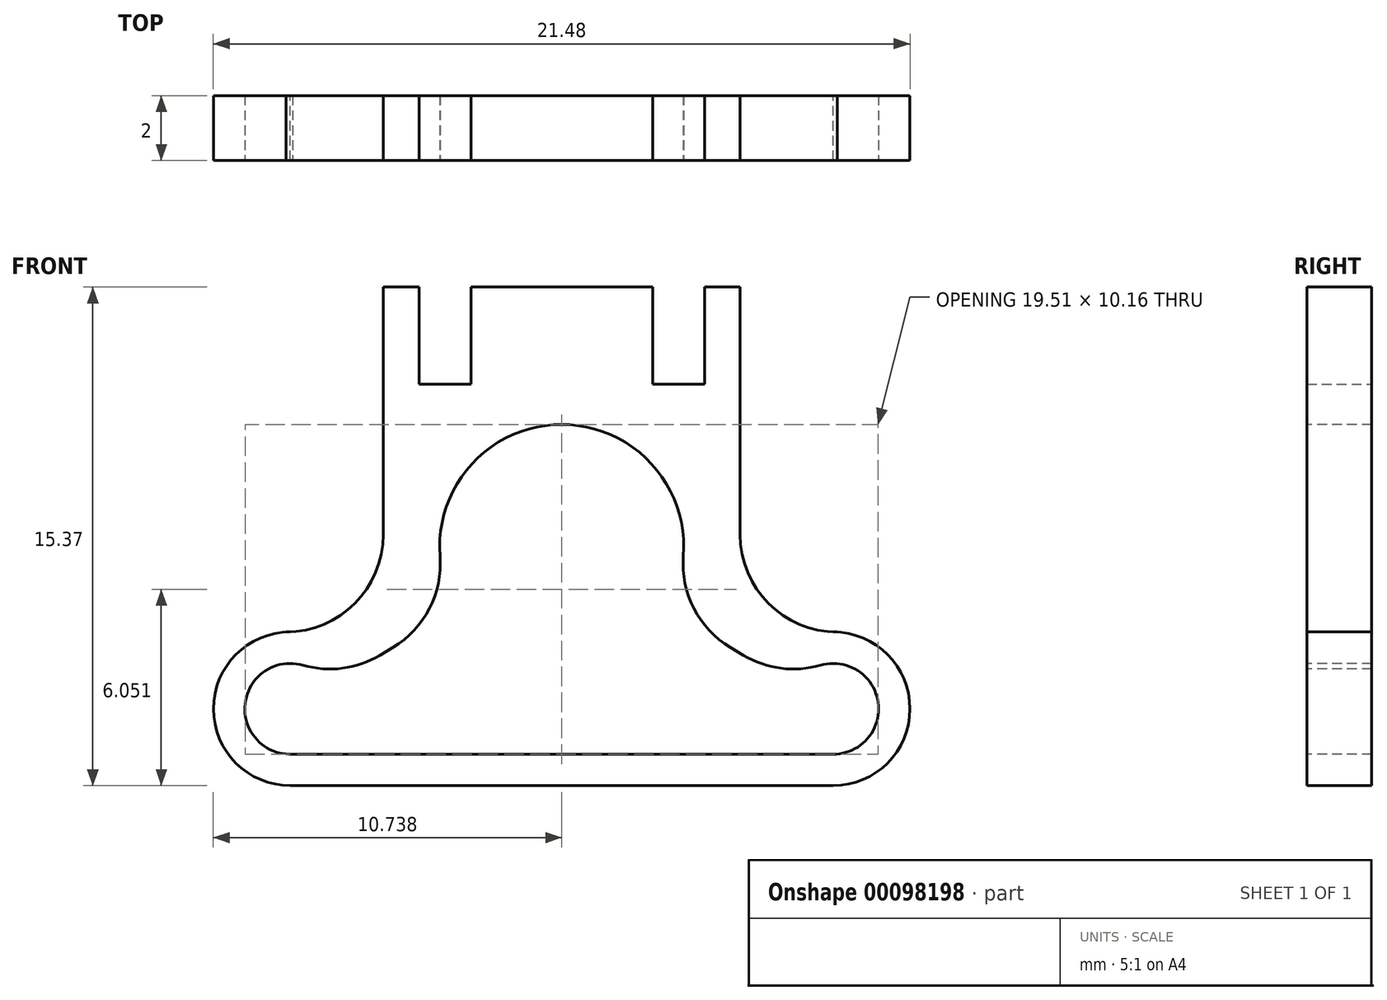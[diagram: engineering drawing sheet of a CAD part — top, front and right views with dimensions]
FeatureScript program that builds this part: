
annotation { "Feature Type Name" : "Feature", "Feature Type Description" : "" }
export const myFeature = defineFeature(function(context is Context, id is Id, definition is map)
    precondition{}
    {
        {
            var Q0;
            Q0=qCreatedBy(makeId("Front.planeOp"),FACE);
            var sketch = newSketch(context, id + "F0", { "sketchPlane" : qUnion([Q0])});
            skLineSegment(sketch, "E0.top", {"start": v(4.4, 5) * mm, "end": v(2.8, 5) * mm});
            skLineSegment(sketch, "E0.left", {"start": v(5.5, 0.37) * mm, "end": v(5.5, 5) * mm});
            skLineSegment(sketch, "E0.right", {"start": v(-5.5, 0.37) * mm, "end": v(-5.5, 5) * mm});
            skPoint(sketch, "E0.middle", {"position": v(0, 0) * mm});
            skLineSegment(sketch, "E1.bottom", {"start": v(8.37, -7.37) * mm, "end": v(-8.37, -7.37) * mm});
            skLineSegment(sketch, "E1.top", {"start": v(8.5, -2.63) * mm, "end": v(8.37, -2.63) * mm});
            skLineSegment(sketch, "E2.trimOffspring", {"start": v(-8.37, -2.63) * mm, "end": v(-8.5, -2.63) * mm});
            skArc(sketch, "E3.filletArc", {"start": v(-8.5, -2.63) * mm, "mid": v(-6.38, -1.75) * mm, "end": v(-5.5, 0.37) * mm});
            skArc(sketch, "E4.filletArc", {"start": v(5.5, 0.37) * mm, "mid": v(6.38, -1.75) * mm, "end": v(8.5, -2.63) * mm});
            skArc(sketch, "E5", {"start": v(-8.37, -2.63) * mm, "mid": v(-10.74, -5) * mm, "end": v(-8.37, -7.37) * mm});
            skArc(sketch, "E6", {"start": v(8.37, -7.37) * mm, "mid": v(10.74, -5) * mm, "end": v(8.37, -2.63) * mm});
            skLineSegment(sketch, "E7.bottom", {"start": v(2.8, 8) * mm, "end": v(-2.8, 8) * mm});
            skLineSegment(sketch, "E7.left", {"start": v(2.8, 8) * mm, "end": v(2.8, 5) * mm});
            skLineSegment(sketch, "E7.right", {"start": v(-2.8, 8) * mm, "end": v(-2.8, 5) * mm});
            skLineSegment(sketch, "E8", {"start": v(-5.5, 5) * mm, "end": v(-5.5, 8) * mm});
            skLineSegment(sketch, "E9", {"start": v(-5.5, 8) * mm, "end": v(-4.4, 8) * mm});
            skLineSegment(sketch, "E10", {"start": v(-4.4, 8) * mm, "end": v(-4.4, 5) * mm});
            skLineSegment(sketch, "E11.trimOffspring", {"start": v(-2.8, 5) * mm, "end": v(-4.4, 5) * mm});
            skLineSegment(sketch, "E12.MirrorCS", {"start": v(5.5, 8) * mm, "end": v(4.4, 8) * mm});
            skLineSegment(sketch, "E13.MirrorCS", {"start": v(4.4, 8) * mm, "end": v(4.4, 5) * mm});
            skLineSegment(sketch, "E14.MirrorCS", {"start": v(5.5, 5) * mm, "end": v(5.5, 8) * mm});
            skSolve(sketch);
        }
        {
            var Q0;
            Q0 = qSketchRegion(id + "F0", true);
            extrude(context, id + "F1", {"entities" : qUnion([Q0]), "depth" : 2 * mm});
        }
        {
            var Q0;
            Q0=makeQuery(id+"F1.opExtrude","CAP_FACE",FACE,{"disambiguationData":[OSD([sQuery(id+"F0.wireOp",EDGE,"E0.top"),sQuery(id+"F0.wireOp",EDGE,"E0.left"),sQuery(id+"F0.wireOp",EDGE,"E0.right"),sQuery(id+"F0.wireOp",EDGE,"E1.bottom"),sQuery(id+"F0.wireOp",EDGE,"E1.top"),sQuery(id+"F0.wireOp",EDGE,"E2.trimOffspring"),sQuery(id+"F0.wireOp",EDGE,"E3.filletArc"),sQuery(id+"F0.wireOp",EDGE,"E4.filletArc"),sQuery(id+"F0.wireOp",EDGE,"E5"),sQuery(id+"F0.wireOp",EDGE,"E6"),sQuery(id+"F0.wireOp",EDGE,"E7.bottom"),sQuery(id+"F0.wireOp",EDGE,"E7.left"),sQuery(id+"F0.wireOp",EDGE,"E7.right"),sQuery(id+"F0.wireOp",EDGE,"E8"),sQuery(id+"F0.wireOp",EDGE,"E9"),sQuery(id+"F0.wireOp",EDGE,"E10"),sQuery(id+"F0.wireOp",EDGE,"E11.trimOffspring"),sQuery(id+"F0.wireOp",EDGE,"E12.MirrorCS"),sQuery(id+"F0.wireOp",EDGE,"E13.MirrorCS"),sQuery(id+"F0.wireOp",EDGE,"E14.MirrorCS")])],"isStart":false});
            var sketch = newSketch(context, id + "F2", { "sketchPlane" : qUnion([Q0])});
            skArc(sketch, "E15", {"start": v(3.75, -0.3) * mm, "mid": v(0, 3.76) * mm, "end": v(-3.75, -0.3) * mm});
            skPoint(sketch, "E16.middle", {"position": v(0, -5.45) * mm});
            skArc(sketch, "E17", {"start": v(-7.98, -3.66) * mm, "mid": v(-9.76, -4.84) * mm, "end": v(-8.3, -6.4) * mm});
            skArc(sketch, "E18", {"start": v(8.37, -6.4) * mm, "mid": v(9.75, -4.8) * mm, "end": v(7.98, -3.66) * mm});
            skLineSegment(sketch, "E19", {"start": v(-8.3, -6.4) * mm, "end": v(8.37, -6.4) * mm});
            skLineSegment(sketch, "E20", {"start": v(-5.2, -3.1) * mm, "end": v(-5.6, -3.35) * mm});
            skLineSegment(sketch, "E21", {"start": v(5.2, -3.1) * mm, "end": v(5.6, -3.35) * mm});
            skPoint(sketch, "E22.visualSharp", {"position": v(-7.17, -4.28) * mm});
            skArc(sketch, "E22.filletArc", {"start": v(-7.98, -3.66) * mm, "mid": v(-6.76, -3.75) * mm, "end": v(-5.6, -3.35) * mm});
            skArc(sketch, "E23.filletArc", {"start": v(-5.2, -3.1) * mm, "mid": v(-4.08, -1.9) * mm, "end": v(-3.75, -0.3) * mm});
            skArc(sketch, "E24.filletArc", {"start": v(3.75, -0.3) * mm, "mid": v(4.08, -1.9) * mm, "end": v(5.2, -3.1) * mm});
            skPoint(sketch, "E25.visualSharp", {"position": v(7.17, -4.28) * mm});
            skArc(sketch, "E25.filletArc", {"start": v(5.6, -3.35) * mm, "mid": v(6.76, -3.75) * mm, "end": v(7.98, -3.66) * mm});
            skSolve(sketch);
        }
        {
            var Q0;
            Q0 = qSketchRegion(id + "F2", true);
            extrude(context, id + "F3", {"entities" : qUnion([Q0]), "operationType" : NewBodyOperationType.REMOVE, "endBound" : BoundingType.THROUGH_ALL, "oppositeDirection" : true, "depth" : 25 * mm});
        }
    });
